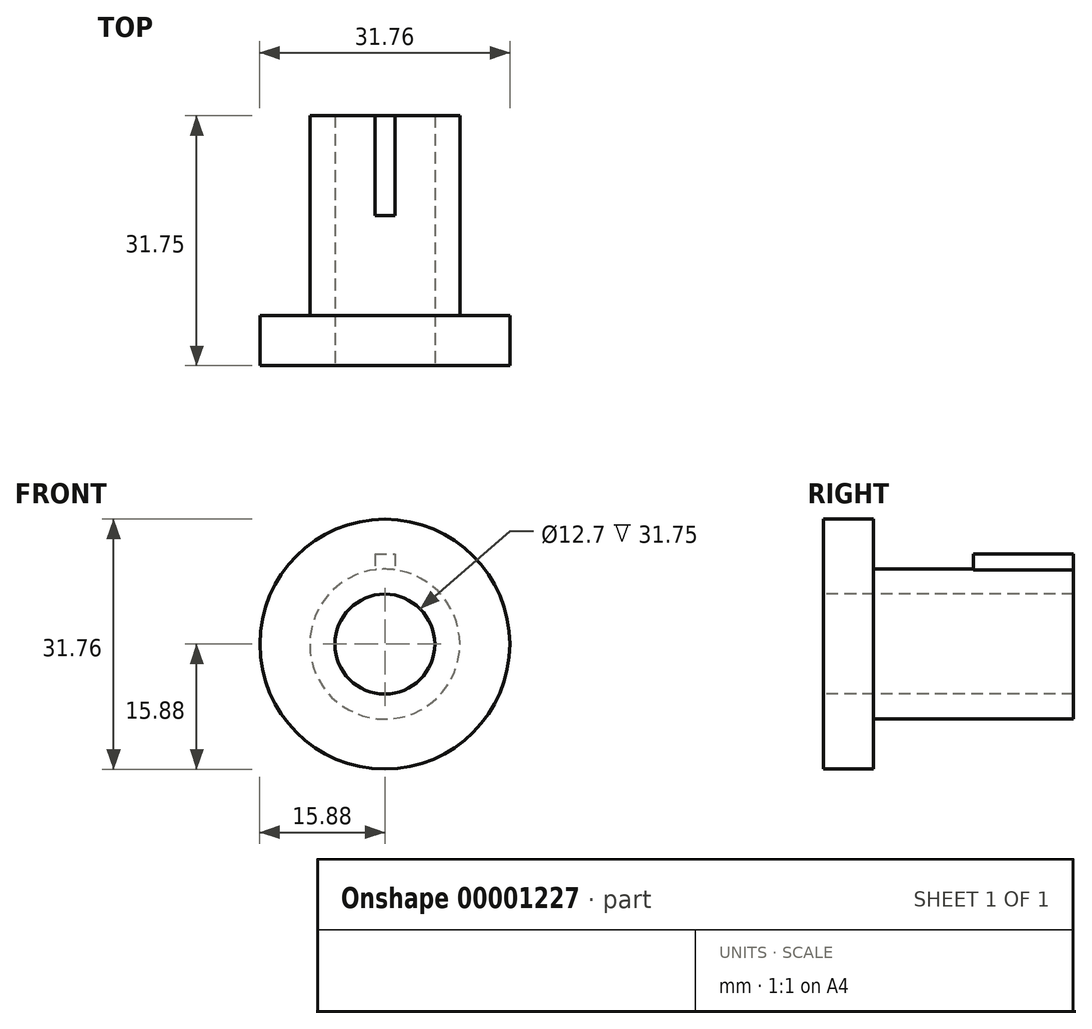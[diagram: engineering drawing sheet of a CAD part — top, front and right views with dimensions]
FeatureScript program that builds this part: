
annotation { "Feature Type Name" : "Feature", "Feature Type Description" : "" }
export const myFeature = defineFeature(function(context is Context, id is Id, definition is map)
    precondition{}
    {
        {
            var Q0;
            Q0=qCreatedBy(makeId("Front.planeOp"),FACE);
            var sketch = newSketch(context, id + "F0", { "sketchPlane" : qUnion([Q0])});
            skCircle(sketch, "E0", {"center": v(0, 0) * mm, "radius": 9.53 * mm});
            skSolve(sketch);
        }
        {
            var Q0;
            Q0 = qSketchRegion(id + "F0", true);
            extrude(context, id + "F1", {"entities" : qUnion([Q0]), "depth" : 25.4 * mm});
        }
        {
            var Q0;
            Q0=makeQuery(id+"F1.opExtrude","CAP_FACE",FACE,{"disambiguationData":[OSD([sQuery(id+"F0.wireOp",EDGE,"E0")])],"isStart":false});
            var sketch = newSketch(context, id + "F2", { "sketchPlane" : qUnion([Q0])});
            skCircle(sketch, "E1", {"center": v(0, 0) * mm, "radius": 15.88 * mm});
            skSolve(sketch);
        }
        {
            var Q0;
            Q0 = qSketchRegion(id + "F2", true);
            extrude(context, id + "F3", {"entities" : qUnion([Q0]), "operationType" : NewBodyOperationType.ADD, "depth" : 6.35 * mm});
        }
        {
            var Q0;
            Q0=makeQuery(id+"F3.opExtrude","CAP_FACE",FACE,{"disambiguationData":[OSD([sQuery(id+"F2.wireOp",EDGE,"E1")])],"isStart":false});
            var sketch = newSketch(context, id + "F4", { "sketchPlane" : qUnion([Q0])});
            skCircle(sketch, "E2", {"center": v(0, 0) * mm, "radius": 6.35 * mm});
            skSolve(sketch);
        }
        {
            var Q0;
            Q0 = qSketchRegion(id + "F4", true);
            var Q1;
            Q1=makeQuery(id+"F1.opExtrude","CAP_FACE",FACE,{"disambiguationData":[OSD([sQuery(id+"F0.wireOp",EDGE,"E0")])],"isStart":true});
            extrude(context, id + "F5", {"entities" : qUnion([Q0, Q1]), "operationType" : NewBodyOperationType.REMOVE, "endBound" : BoundingType.THROUGH_ALL, "oppositeDirection" : true, "depth" : 25.4 * mm});
        }
        {
            var Q0;
            Q0=makeQuery(id+"F1.opExtrude","CAP_FACE",FACE,{"disambiguationData":[OSD([sQuery(id+"F0.wireOp",EDGE,"E0")])],"isStart":true});
            var sketch = newSketch(context, id + "F6", { "sketchPlane" : qUnion([Q0])});
            skLineSegment(sketch, "E3.rect.bottom", {"start": v(1.27, 11.43) * mm, "end": v(-1.27, 11.43) * mm});
            skLineSegment(sketch, "E3.rect.left", {"start": v(1.27, 11.43) * mm, "end": v(1.27, 9.44) * mm});
            skLineSegment(sketch, "E3.rect.right", {"start": v(-1.27, 11.43) * mm, "end": v(-1.27, 9.44) * mm});
            skPoint(sketch, "E3.rect.middle", {"position": v(0, 9.53) * mm});
            skArc(sketch, "E4", {"start": v(1.27, 9.44) * mm, "mid": v(0, 9.53) * mm, "end": v(-1.27, 9.44) * mm});
            skPoint(sketch, "E3.rect.top.end.orphan", {"position": v(-1.27, 7.62) * mm});
            skPoint(sketch, "E5.orphan", {"position": v(1.27, 7.62) * mm});
            skSolve(sketch);
        }
        {
            var Q0;
            Q0 = qSketchRegion(id + "F6", true);
            extrude(context, id + "F7", {"entities" : qUnion([Q0]), "oppositeDirection" : true, "depth" : 12.7 * mm});
        }
    });
